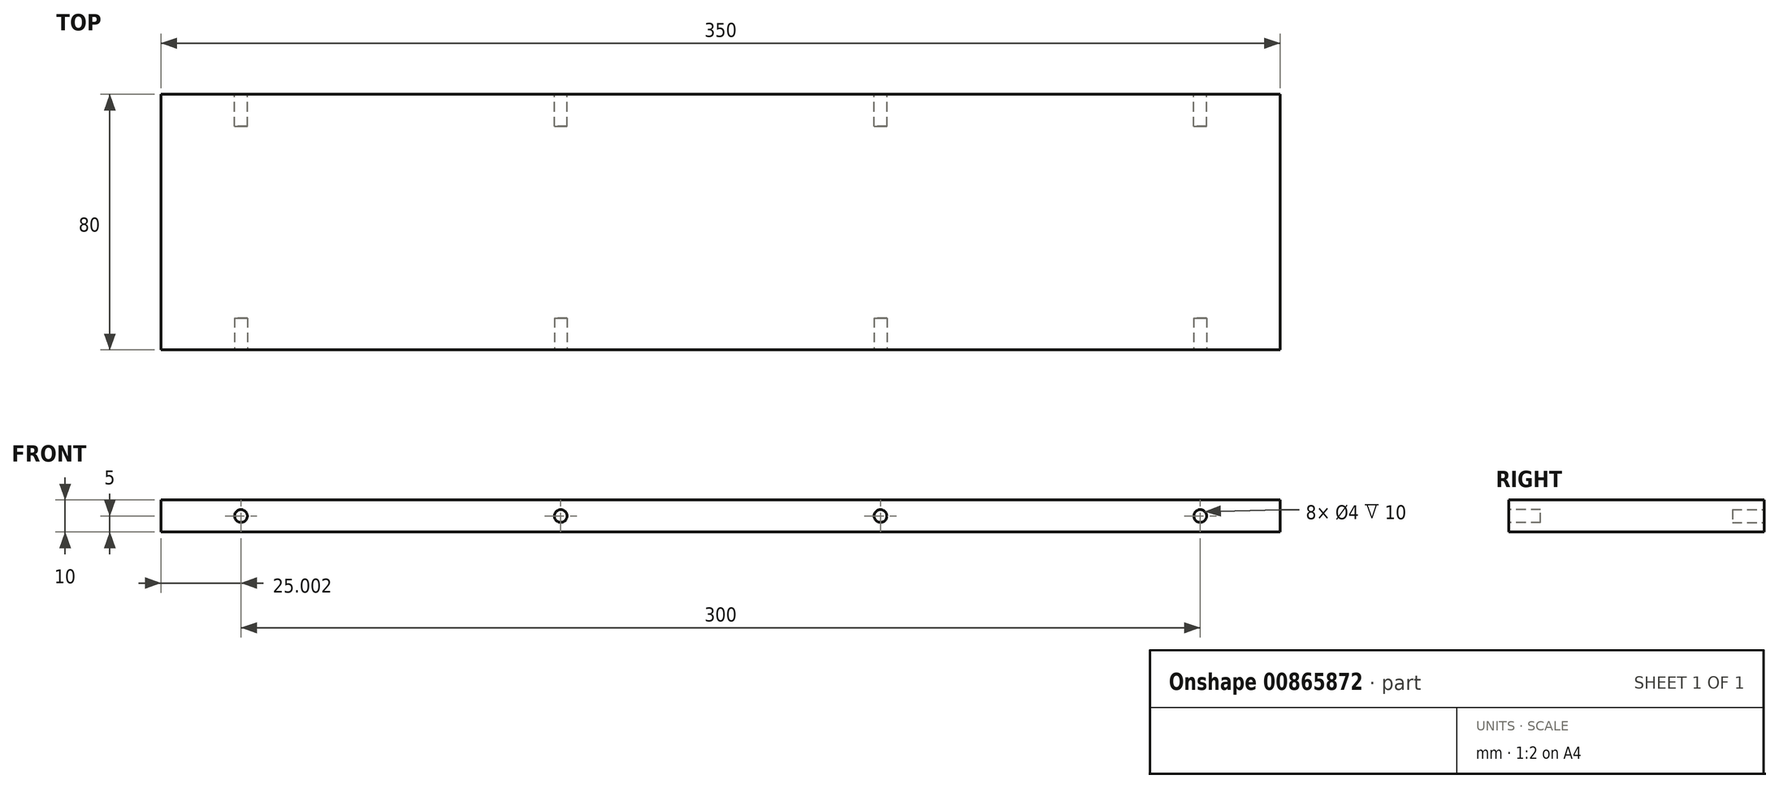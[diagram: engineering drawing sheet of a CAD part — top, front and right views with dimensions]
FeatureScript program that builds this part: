
annotation { "Feature Type Name" : "Feature", "Feature Type Description" : "" }
export const myFeature = defineFeature(function(context is Context, id is Id, definition is map)
    precondition{}
    {
        {
            var Q0;
            Q0=qCreatedBy(makeId("Top.planeOp"),FACE);
            var sketch = newSketch(context, id + "F0", { "sketchPlane" : qUnion([Q0])});
            skLineSegment(sketch, "E0.bottom", {"start": v(-195.67, -36.19) * mm, "end": v(154.33, -36.19) * mm});
            skLineSegment(sketch, "E0.top", {"start": v(-195.67, -116.19) * mm, "end": v(154.33, -116.19) * mm});
            skLineSegment(sketch, "E0.left", {"start": v(-195.67, -36.19) * mm, "end": v(-195.67, -116.19) * mm});
            skLineSegment(sketch, "E0.right", {"start": v(154.33, -36.19) * mm, "end": v(154.33, -116.19) * mm});
            skSolve(sketch);
        }
        {
            var Q0;
            Q0 = qSketchRegion(id + "F0", true);
            extrude(context, id + "F1", {"entities" : qUnion([Q0]), "depth" : 10 * mm, "offsetDistance" : 25 * mm});
        }
        {
            var Q0;
            Q0=makeQuery(id+"F1.opExtrude","SWEPT_FACE",FACE,{"disambiguationData":[OSD([sQuery(id+"F0.wireOp",EDGE,"E0.top")])]});
            var sketch = newSketch(context, id + "F2", { "sketchPlane" : qUnion([Q0])});
            skCircle(sketch, "E1", {"center": v(-170.67, 5) * mm, "radius": 2 * mm});
            skPoint(sketch, "E1.centerSnap0", {"position": v(-195.67, 5) * mm});
            skCircle(sketch, "E2", {"center": v(-70.67, 5) * mm, "radius": 2 * mm});
            skCircle(sketch, "E3", {"center": v(29.33, 5) * mm, "radius": 2 * mm});
            skCircle(sketch, "E4", {"center": v(129.33, 5) * mm, "radius": 2 * mm});
            skSolve(sketch);
        }
        {
            var Q0;
            Q0 = qSketchRegion(id + "F2", true);
            extrude(context, id + "F3", {"entities" : qUnion([Q0]), "operationType" : NewBodyOperationType.REMOVE, "oppositeDirection" : true, "depth" : 10 * mm, "offsetDistance" : 25 * mm});
        }
        {
            var Q0;
            Q0=makeQuery(id+"F1.opExtrude","SWEPT_FACE",FACE,{"disambiguationData":[OSD([sQuery(id+"F0.wireOp",EDGE,"E0.bottom")])]});
            var sketch = newSketch(context, id + "F4", { "sketchPlane" : qUnion([Q0])});
            skCircle(sketch, "E5", {"center": v(170.67, 5) * mm, "radius": 2 * mm});
            skPoint(sketch, "E5.centerSnap0", {"position": v(195.67, 5) * mm});
            skCircle(sketch, "E6", {"center": v(70.67, 5) * mm, "radius": 2 * mm});
            skCircle(sketch, "E7", {"center": v(-29.33, 5) * mm, "radius": 2 * mm});
            skCircle(sketch, "E8", {"center": v(-129.33, 5) * mm, "radius": 2 * mm});
            skSolve(sketch);
        }
        {
            var Q0;
            Q0 = qSketchRegion(id + "F4", true);
            extrude(context, id + "F5", {"entities" : qUnion([Q0]), "operationType" : NewBodyOperationType.REMOVE, "oppositeDirection" : true, "depth" : 10 * mm, "offsetDistance" : 25 * mm});
        }
    });
